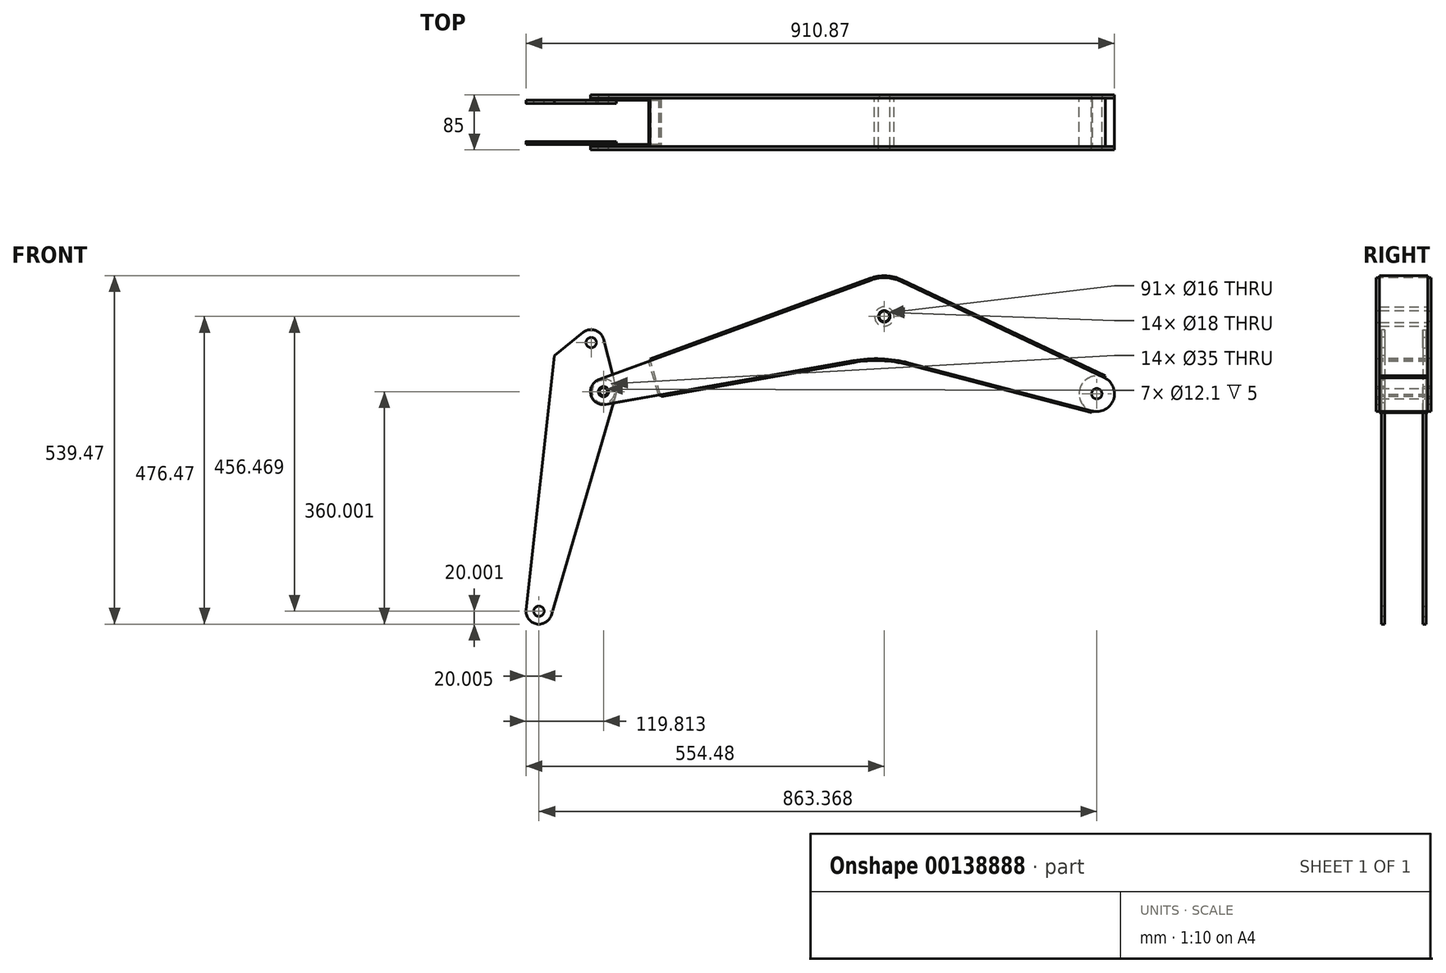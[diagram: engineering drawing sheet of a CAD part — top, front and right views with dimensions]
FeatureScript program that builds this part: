
annotation { "Feature Type Name" : "Feature", "Feature Type Description" : "" }
export const myFeature = defineFeature(function(context is Context, id is Id, definition is map)
    precondition{}
    {
        {
            var Q0;
            Q0=qCreatedBy(makeId("Front.planeOp"),FACE);
            var sketch = newSketch(context, id + "F0", { "sketchPlane" : qUnion([Q0])});
            skCircle(sketch, "E0", {"center": v(0, 0) * mm, "radius": 60 * mm});
            skLineSegment(sketch, "E1", {"start": v(0, 0) * mm, "end": v(-434.67, -116.47) * mm, "construction": true});
            skCircle(sketch, "E2", {"center": v(-434.67, -116.47) * mm, "radius": 20 * mm});
            skLineSegment(sketch, "E3", {"start": v(0, 0) * mm, "end": v(328.9, -119.7) * mm, "construction": true});
            skCircle(sketch, "E4", {"center": v(328.9, -119.7) * mm, "radius": 27.5 * mm});
            skLineSegment(sketch, "E5", {"start": v(-20.62, 56.35) * mm, "end": v(-441.54, -97.69) * mm});
            skLineSegment(sketch, "E6", {"start": v(-47.69, -68.42) * mm, "end": v(-431.19, -136.16) * mm});
            skLineSegment(sketch, "E7", {"start": v(37.7, -71.9) * mm, "end": v(321.93, -146.31) * mm});
            skLineSegment(sketch, "E8", {"start": v(25.67, 54.23) * mm, "end": v(340.66, -94.85) * mm});
            skPoint(sketch, "E9", {"position": v(-4.61, -60.81) * mm});
            skPoint(sketch, "E10.orphan", {"position": v(0, -60) * mm});
            skArc(sketch, "E11.filletArc", {"start": v(37.7, -71.9) * mm, "mid": v(-4.8, -65.54) * mm, "end": v(-47.69, -68.42) * mm});
            skCircle(sketch, "E12", {"center": v(0, 0) * mm, "radius": 8 * mm});
            skCircle(sketch, "E13", {"center": v(328.9, -119.7) * mm, "radius": 8 * mm});
            skCircle(sketch, "E14", {"center": v(-434.67, -116.47) * mm, "radius": 8 * mm});
            skCircle(sketch, "E15", {"center": v(328.9, -119.7) * mm, "radius": 6.05 * mm});
            skCircle(sketch, "E16", {"center": v(328.9, -119.7) * mm, "radius": 22.5 * mm});
            skCircle(sketch, "E17", {"center": v(-434.67, -116.47) * mm, "radius": 6.05 * mm});
            skCircle(sketch, "E18", {"center": v(-434.67, -116.47) * mm, "radius": 17.5 * mm});
            skCircle(sketch, "E19", {"center": v(0, 0) * mm, "radius": 6.05 * mm});
            skCircle(sketch, "E20", {"center": v(0, 0) * mm, "radius": 9 * mm});
            skCircle(sketch, "E21", {"center": v(0, 0) * mm, "radius": 15 * mm});
            skSolve(sketch);
        }
        {
            var Q0;
            Q0 = qSketchRegion(id + "FwEDvxsUyDdSrLS_0", true);
            var Q1;
            Q1=makeQuery(id+"F0.imprint","IMPRINT",FACE,{"disambiguationData":[TD([[makeQuery(id+"F0.imprint","IMPRINT",EDGE,{"derivedFrom":sQuery(id+"F0.wireOp",EDGE,"E14")}),-1.0]])]});
            extrude(context, id + "F1", {"entities" : qUnion([Q0, Q1]), "depth" : 5 * mm});
        }
        {
            var Q0;
            Q0 = qSketchRegion(id + "F0", true);
            var Q1;
            Q1=makeQuery(id+"F0.imprint","IMPRINT",FACE,{"disambiguationData":[TD([[makeQuery(id+"F0.imprint","IMPRINT",EDGE,{"derivedFrom":sQuery(id+"F0.wireOp",EDGE,"E13")}),-1.0]])]});
            var Q2;
            Q2=makeQuery(id+"F0.imprint","IMPRINT",FACE,{"disambiguationData":[TD([[makeQuery(id+"F0.imprint","IMPRINT",EDGE,{"derivedFrom":sQuery(id+"F0.wireOp",EDGE,"E12")}),-1.0]])]});
            var Q3;
            Q3=makeQuery(id+"F0.imprint","IMPRINT",FACE,{"disambiguationData":[TD([[makeQuery(id+"F0.imprint","IMPRINT",EDGE,{"derivedFrom":sQuery(id+"F0.wireOp",EDGE,"E14")}),-1.0]])]});
            var Q4;
            Q4=makeQuery(id+"F0.imprint","IMPRINT",FACE,{"disambiguationData":[TD([[makeQuery(id+"F0.imprint","IMPRINT",EDGE,{"derivedFrom":sQuery(id+"F0.wireOp",EDGE,"E20")}),-1.0]])]});
            extrude(context, id + "F2", {"entities" : qUnion([Q0, Q1, Q2, Q3, Q4]), "oppositeDirection" : true, "depth" : 5 * mm});
        }
        {
            var Q0;
            Q0=makeQuery(id+"F2.opExtrude","CAP_FACE",FACE,{"disambiguationData":[OSD([sQuery(id+"F0.wireOp",EDGE,"E0"),sQuery(id+"F0.wireOp",EDGE,"E2"),sQuery(id+"F0.wireOp",EDGE,"E4"),sQuery(id+"F0.wireOp",EDGE,"E5"),sQuery(id+"F0.wireOp",EDGE,"E6"),sQuery(id+"F0.wireOp",EDGE,"E7"),sQuery(id+"F0.wireOp",EDGE,"E8"),sQuery(id+"F0.wireOp",EDGE,"E11.filletArc"),sQuery(id+"F0.wireOp",EDGE,"E12"),sQuery(id+"F0.wireOp",EDGE,"E13"),sQuery(id+"F0.wireOp",EDGE,"E14")])],"isStart":true});
            cPlane(context, id + "F3", {"entities" : qUnion([Q0]), "cplaneType" : CPlaneType.OFFSET, "offset" : 75 * mm, "width" : 150 * mm, "height" : 150 * mm});
        }
        {
            var Q0;
            Q0=qCreatedBy(id+"F3.planeOp",FACE);
            var sketch = newSketch(context, id + "F4", { "sketchPlane" : qUnion([Q0])});
            skArc(sketch, "E22.0.0", {"start": v(25.67, 54.23) * mm, "mid": v(2.74, 59.94) * mm, "end": v(-20.62, 56.35) * mm});
            skLineSegment(sketch, "E22.0.1", {"start": v(-20.62, 56.35) * mm, "end": v(-441.54, -97.69) * mm});
            skArc(sketch, "E22.0.2", {"start": v(-441.54, -97.69) * mm, "mid": v(-453.98, -121.66) * mm, "end": v(-431.19, -136.16) * mm});
            skLineSegment(sketch, "E22.0.3", {"start": v(-431.19, -136.16) * mm, "end": v(-47.69, -68.42) * mm});
            skArc(sketch, "E22.0.4", {"start": v(-47.69, -68.42) * mm, "mid": v(-4.8, -65.54) * mm, "end": v(37.7, -71.9) * mm});
            skLineSegment(sketch, "E22.0.5", {"start": v(37.7, -71.9) * mm, "end": v(321.93, -146.31) * mm});
            skArc(sketch, "E22.0.6", {"start": v(321.93, -146.31) * mm, "mid": v(354.73, -129.11) * mm, "end": v(340.66, -94.85) * mm});
            skLineSegment(sketch, "E22.0.7", {"start": v(340.66, -94.85) * mm, "end": v(25.67, 54.23) * mm});
            skCircle(sketch, "E23.0", {"center": v(-434.67, -116.47) * mm, "radius": 8 * mm});
            skCircle(sketch, "E24.0", {"center": v(0, 0) * mm, "radius": 8 * mm});
            skCircle(sketch, "E24.1", {"center": v(328.9, -119.7) * mm, "radius": 8 * mm});
            skCircle(sketch, "E25.0", {"center": v(0, 0) * mm, "radius": 6.05 * mm});
            skCircle(sketch, "E25.1", {"center": v(0, 0) * mm, "radius": 9 * mm});
            skCircle(sketch, "E26.0", {"center": v(328.9, -119.7) * mm, "radius": 6.05 * mm});
            skCircle(sketch, "E26.1", {"center": v(328.9, -119.7) * mm, "radius": 22.5 * mm});
            skCircle(sketch, "E27.0", {"center": v(-434.67, -116.47) * mm, "radius": 6.05 * mm});
            skCircle(sketch, "E27.1", {"center": v(-434.67, -116.47) * mm, "radius": 17.5 * mm});
            skSolve(sketch);
        }
        {
            var Q0;
            Q0 = qSketchRegion(id + "F4", true);
            var Q1;
            Q1=makeQuery(id+"F4.imprint","IMPRINT",FACE,{"disambiguationData":[TD([[makeQuery(id+"F4.imprint","IMPRINT",EDGE,{"derivedFrom":sQuery(id+"F4.wireOp",EDGE,"E24.1")}),-1.0]])]});
            var Q2;
            Q2=makeQuery(id+"F4.imprint","IMPRINT",FACE,{"disambiguationData":[TD([[makeQuery(id+"F4.imprint","IMPRINT",EDGE,{"derivedFrom":sQuery(id+"F4.wireOp",EDGE,"E23.0")}),-1.0]])]});
            extrude(context, id + "F5", {"entities" : qUnion([Q0, Q1, Q2]), "depth" : 5 * mm});
        }
        {
            var Q0;
            Q0=makeQuery(id+"F0.imprint","IMPRINT",FACE,{"disambiguationData":[TD([[makeQuery(id+"F0.imprint","IMPRINT",EDGE,{"derivedFrom":sQuery(id+"F0.wireOp",EDGE,"E13")}),-1.0]])]});
            var Q1;
            Q1=makeQuery(id+"F0.imprint","IMPRINT",FACE,{"disambiguationData":[TD([[makeQuery(id+"F0.imprint","IMPRINT",EDGE,{"derivedFrom":sQuery(id+"F0.wireOp",EDGE,"E16")}),-1.0]])]});
            var Q2;
            Q2=makeQuery(id+"F5.opExtrude","CAP_FACE",FACE,{"disambiguationData":[OSD([sQuery(id+"F4.wireOp",EDGE,"E22.0.0"),sQuery(id+"F4.wireOp",EDGE,"E22.0.1"),sQuery(id+"F4.wireOp",EDGE,"E22.0.2"),sQuery(id+"F4.wireOp",EDGE,"E22.0.3"),sQuery(id+"F4.wireOp",EDGE,"E22.0.4"),sQuery(id+"F4.wireOp",EDGE,"E22.0.5"),sQuery(id+"F4.wireOp",EDGE,"E22.0.6"),sQuery(id+"F4.wireOp",EDGE,"E22.0.7"),sQuery(id+"F4.wireOp",EDGE,"E23.0"),sQuery(id+"F4.wireOp",EDGE,"E24.1"),sQuery(id+"F4.wireOp",EDGE,"E25.1")])],"isStart":true});
            extrude(context, id + "F6", {"entities" : qUnion([Q0, Q1]), "endBound" : BoundingType.UP_TO_SURFACE, "endBoundEntityFace" : qUnion([Q2]), "depth" : 25 * mm});
        }
        {
            var Q0;
            Q0=makeQuery(id+"F0.imprint","IMPRINT",FACE,{"disambiguationData":[TD([[makeQuery(id+"F0.imprint","IMPRINT",EDGE,{"derivedFrom":sQuery(id+"F0.wireOp",EDGE,"E20")}),-1.0]])]});
            var Q1;
            Q1=makeQuery(id+"F5.opExtrude","CAP_FACE",FACE,{"disambiguationData":[OSD([sQuery(id+"F4.wireOp",EDGE,"E22.0.0"),sQuery(id+"F4.wireOp",EDGE,"E22.0.1"),sQuery(id+"F4.wireOp",EDGE,"E22.0.2"),sQuery(id+"F4.wireOp",EDGE,"E22.0.3"),sQuery(id+"F4.wireOp",EDGE,"E22.0.4"),sQuery(id+"F4.wireOp",EDGE,"E22.0.5"),sQuery(id+"F4.wireOp",EDGE,"E22.0.6"),sQuery(id+"F4.wireOp",EDGE,"E22.0.7"),sQuery(id+"F4.wireOp",EDGE,"E23.0"),sQuery(id+"F4.wireOp",EDGE,"E24.1"),sQuery(id+"F4.wireOp",EDGE,"E25.1")])],"isStart":true});
            extrude(context, id + "F7", {"entities" : qUnion([Q0]), "endBound" : BoundingType.UP_TO_SURFACE, "endBoundEntityFace" : qUnion([Q1]), "depth" : 25 * mm});
        }
        {
            var Q0;
            Q0=makeQuery(id+"F4.imprint","IMPRINT",FACE,{"disambiguationData":[TD([[makeQuery(id+"F4.imprint","IMPRINT",EDGE,{"derivedFrom":sQuery(id+"F4.wireOp",EDGE,"E22.0.0")}),1.0]])]});
            var sketch = newSketch(context, id + "F8", { "sketchPlane" : qUnion([Q0])});
            skLineSegment(sketch, "E28.0", {"start": v(-20.62, 56.35) * mm, "end": v(-441.54, -97.69) * mm});
            skArc(sketch, "E28.1", {"start": v(25.67, 54.23) * mm, "mid": v(2.74, 59.94) * mm, "end": v(-20.62, 56.35) * mm});
            skLineSegment(sketch, "E28.2", {"start": v(340.66, -94.85) * mm, "end": v(25.67, 54.23) * mm});
            skLineSegment(sketch, "E28.3", {"start": v(37.7, -71.9) * mm, "end": v(321.93, -146.31) * mm});
            skArc(sketch, "E28.4", {"start": v(-47.69, -68.42) * mm, "mid": v(-4.8, -65.54) * mm, "end": v(37.7, -71.9) * mm});
            skLineSegment(sketch, "E28.5", {"start": v(-431.19, -136.16) * mm, "end": v(-47.69, -68.42) * mm});
            skLineSegment(sketch, "E29.0", {"start": v(-21.65, 59.16) * mm, "end": v(-362.75, -65.66) * mm});
            skArc(sketch, "E29.1", {"start": v(26.95, 56.94) * mm, "mid": v(2.87, 62.93) * mm, "end": v(-21.65, 59.16) * mm});
            skLineSegment(sketch, "E29.2", {"start": v(341.94, -92.14) * mm, "end": v(26.95, 56.94) * mm});
            skLineSegment(sketch, "E30.0", {"start": v(36.94, -74.8) * mm, "end": v(321.17, -149.21) * mm});
            skArc(sketch, "E30.1", {"start": v(-47.16, -71.38) * mm, "mid": v(-4.93, -68.54) * mm, "end": v(36.94, -74.8) * mm});
            skLineSegment(sketch, "E30.2", {"start": v(-345.67, -124.1) * mm, "end": v(-47.16, -71.38) * mm});
            skLineSegment(sketch, "E31", {"start": v(341.94, -92.14) * mm, "end": v(340.66, -94.85) * mm});
            skLineSegment(sketch, "E32", {"start": v(321.93, -146.31) * mm, "end": v(321.17, -149.21) * mm});
            skLineSegment(sketch, "E33", {"start": v(-362.75, -65.66) * mm, "end": v(-361.72, -68.48) * mm});
            skLineSegment(sketch, "E34", {"start": v(-346.19, -121.15) * mm, "end": v(-345.67, -124.1) * mm});
            skLineSegment(sketch, "E35", {"start": v(-362.75, -65.66) * mm, "end": v(-345.67, -124.1) * mm});
            skLineSegment(sketch, "E36", {"start": v(-362.75, -65.66) * mm, "end": v(-365.56, -66.69) * mm});
            skLineSegment(sketch, "E37", {"start": v(-345.67, -124.1) * mm, "end": v(-348.62, -124.63) * mm});
            skLineSegment(sketch, "E38", {"start": v(-348.62, -124.63) * mm, "end": v(-365.56, -66.69) * mm});
            skSolve(sketch);
        }
        {
            var Q0;
            {var subQ0=sQuery(id+"F8.wireOp",EDGE,"E28.1");Q0=makeQuery(id+"F8.imprint","IMPRINT",FACE,{"disambiguationData":[TD([[makeQuery(id+"F8.imprint","IMPRINT",EDGE,{"derivedFrom":subQ0}),-1.0]])]});}
            var Q1;
            Q1=makeQuery(id+"F2.opExtrude","CAP_FACE",FACE,{"disambiguationData":[OSD([sQuery(id+"F0.wireOp",EDGE,"E0"),sQuery(id+"F0.wireOp",EDGE,"E2"),sQuery(id+"F0.wireOp",EDGE,"E4"),sQuery(id+"F0.wireOp",EDGE,"E5"),sQuery(id+"F0.wireOp",EDGE,"E6"),sQuery(id+"F0.wireOp",EDGE,"E7"),sQuery(id+"F0.wireOp",EDGE,"E8"),sQuery(id+"F0.wireOp",EDGE,"E11.filletArc"),sQuery(id+"F0.wireOp",EDGE,"E12"),sQuery(id+"F0.wireOp",EDGE,"E13"),sQuery(id+"F0.wireOp",EDGE,"E14")])],"isStart":true});
            extrude(context, id + "F9", {"entities" : qUnion([Q0]), "endBound" : BoundingType.UP_TO_SURFACE, "oppositeDirection" : true, "endBoundEntityFace" : qUnion([Q1]), "depth" : 25 * mm});
        }
        {
            var Q0;
            Q0=makeQuery(id+"F8.imprint","IMPRINT",FACE,{"disambiguationData":[TD([[makeQuery(id+"F8.imprint","IMPRINT",EDGE,{"derivedFrom":sQuery(id+"F8.wireOp",EDGE,"E28.3")}),-1.0]])]});
            var Q1;
            Q1=makeQuery(id+"F2.opExtrude","CAP_FACE",FACE,{"disambiguationData":[OSD([sQuery(id+"F0.wireOp",EDGE,"E0"),sQuery(id+"F0.wireOp",EDGE,"E2"),sQuery(id+"F0.wireOp",EDGE,"E4"),sQuery(id+"F0.wireOp",EDGE,"E5"),sQuery(id+"F0.wireOp",EDGE,"E6"),sQuery(id+"F0.wireOp",EDGE,"E7"),sQuery(id+"F0.wireOp",EDGE,"E8"),sQuery(id+"F0.wireOp",EDGE,"E11.filletArc"),sQuery(id+"F0.wireOp",EDGE,"E12"),sQuery(id+"F0.wireOp",EDGE,"E13"),sQuery(id+"F0.wireOp",EDGE,"E14")])],"isStart":true});
            extrude(context, id + "F10", {"entities" : qUnion([Q0]), "endBound" : BoundingType.UP_TO_SURFACE, "oppositeDirection" : true, "endBoundEntityFace" : qUnion([Q1]), "depth" : 25 * mm});
        }
        {
            var Q0;
            {var subQ0=sQuery(id+"F8.wireOp",EDGE,"E38");var subQ1=sQuery(id+"F8.wireOp",EDGE,"E28.0");var subQ2=makeQuery(id+"F8.imprint","INTERSECT",VERTEX,{"derivedFrom":[subQ1,subQ0]});Q0=makeQuery(id+"F8.imprint","IMPRINT",FACE,{"disambiguationData":[TD([[makeQuery(id+"F8.imprint","IMPRINT",EDGE,{"disambiguationData":[TD([[subQ2,1.0]])],"derivedFrom":subQ1}),1.0]])]});}
            var Q1;
            Q1=makeQuery(id+"F2.opExtrude","CAP_FACE",FACE,{"disambiguationData":[OSD([sQuery(id+"F0.wireOp",EDGE,"E0"),sQuery(id+"F0.wireOp",EDGE,"E2"),sQuery(id+"F0.wireOp",EDGE,"E4"),sQuery(id+"F0.wireOp",EDGE,"E5"),sQuery(id+"F0.wireOp",EDGE,"E6"),sQuery(id+"F0.wireOp",EDGE,"E7"),sQuery(id+"F0.wireOp",EDGE,"E8"),sQuery(id+"F0.wireOp",EDGE,"E11.filletArc"),sQuery(id+"F0.wireOp",EDGE,"E12"),sQuery(id+"F0.wireOp",EDGE,"E13"),sQuery(id+"F0.wireOp",EDGE,"E14")])],"isStart":true});
            extrude(context, id + "F11", {"entities" : qUnion([Q0]), "endBound" : BoundingType.UP_TO_SURFACE, "oppositeDirection" : true, "endBoundEntityFace" : qUnion([Q1]), "depth" : 25 * mm});
        }
        {
            var Q0;
            {var subQ0=makeQuery(id+"F4.imprint","IMPRINT",EDGE,{"derivedFrom":sQuery(id+"F4.wireOp",EDGE,"E22.0.2")});Q0=makeQuery(id+"F8.imprint","IMPRINT",FACE,{"disambiguationData":[TD([[makeQuery(id+"F8.imprint","IMPRINT",EDGE,{"derivedFrom":subQ0}),1.0]])]});}
            var Q1;
            Q1=makeQuery(id+"F4.imprint","IMPRINT",FACE,{"disambiguationData":[TD([[makeQuery(id+"F4.imprint","IMPRINT",EDGE,{"derivedFrom":sQuery(id+"F4.wireOp",EDGE,"E23.0")}),-1.0]])]});
            extrude(context, id + "F12", {"entities" : qUnion([Q0, Q1]), "oppositeDirection" : true, "depth" : 3 * mm});
        }
        {
            var Q0;
            {var subQ0=sQuery(id+"F0.wireOp",EDGE,"E5");Q0=makeQuery(id+"F0.imprint","IMPRINT",FACE,{"disambiguationData":[TD([[makeQuery(id+"F0.imprint","IMPRINT",EDGE,{"derivedFrom":subQ0}),1.0]])]});}
            var sketch = newSketch(context, id + "F13", { "sketchPlane" : qUnion([Q0])});
            skLineSegment(sketch, "E39.0", {"start": v(-364.72, -69.58) * mm, "end": v(-349.47, -121.73) * mm});
            skLineSegment(sketch, "E39.1", {"start": v(-20.62, 56.35) * mm, "end": v(-441.54, -97.69) * mm});
            skLineSegment(sketch, "E39.2", {"start": v(-47.69, -68.42) * mm, "end": v(-431.19, -136.16) * mm});
            skCircle(sketch, "E39.3", {"center": v(-434.67, -116.47) * mm, "radius": 20 * mm});
            skSolve(sketch);
        }
        {
            var Q0;
            {var subQ0=sQuery(id+"F13.wireOp",EDGE,"E39.0");Q0=makeQuery(id+"F13.imprint","IMPRINT",FACE,{"disambiguationData":[TD([[makeQuery(id+"F13.imprint","IMPRINT",EDGE,{"derivedFrom":subQ0}),-1.0]])]});}
            var Q1;
            Q1=makeQuery(id+"F0.imprint","IMPRINT",FACE,{"disambiguationData":[TD([[makeQuery(id+"F0.imprint","IMPRINT",EDGE,{"derivedFrom":sQuery(id+"F0.wireOp",EDGE,"E14")}),-1.0]])]});
            var Q2;
            Q2=makeQuery(id+"F0.imprint","IMPRINT",FACE,{"disambiguationData":[TD([[makeQuery(id+"F0.imprint","IMPRINT",EDGE,{"derivedFrom":sQuery(id+"F0.wireOp",EDGE,"E18")}),-1.0]])]});
            extrude(context, id + "F14", {"entities" : qUnion([Q0, Q1, Q2]), "depth" : 3 * mm});
        }
        {
            var Q0;
            Q0=makeQuery(id+"F12.opExtrude","CAP_FACE",FACE,{"disambiguationData":[OSD([sQuery(id+"F4.wireOp",EDGE,"E22.0.2"),sQuery(id+"F4.wireOp",EDGE,"E27.1"),sQuery(id+"F8.wireOp",EDGE,"E28.0"),sQuery(id+"F8.wireOp",EDGE,"E28.5"),sQuery(id+"F8.wireOp",EDGE,"E38")])],"isStart":false});
            cPlane(context, id + "F15", {"entities" : qUnion([Q0]), "cplaneType" : CPlaneType.OFFSET, "offset" : 0 * mm, "width" : 150 * mm, "height" : 150 * mm});
        }
        {
            var Q0;
            Q0=qCreatedBy(id+"F15.planeOp",FACE);
            var sketch = newSketch(context, id + "F16", { "sketchPlane" : qUnion([Q0])});
            skCircle(sketch, "E40.0", {"center": v(434.67, -116.47) * mm, "radius": 6.05 * mm});
            skCircle(sketch, "E40.1", {"center": v(434.67, -116.47) * mm, "radius": 8 * mm});
            skCircle(sketch, "E40.2", {"center": v(434.67, -116.47) * mm, "radius": 17.5 * mm});
            skCircle(sketch, "E40.3", {"center": v(434.67, -116.47) * mm, "radius": 20 * mm});
            skCircle(sketch, "E40.4", {"center": v(453.67, -40.47) * mm, "radius": 20 * mm});
            skLineSegment(sketch, "E40.5", {"start": v(434.26, -35.62) * mm, "end": v(415.26, -111.62) * mm});
            skCircle(sketch, "E40.6", {"center": v(534.48, -456.47) * mm, "radius": 20 * mm});
            skLineSegment(sketch, "E40.7", {"start": v(466.16, -24.85) * mm, "end": v(510.67, -60.47) * mm});
            skLineSegment(sketch, "E40.8", {"start": v(510.67, -60.47) * mm, "end": v(554.35, -454.26) * mm});
            skLineSegment(sketch, "E40.9", {"start": v(515.29, -462.1) * mm, "end": v(415.48, -122.1) * mm});
            skCircle(sketch, "E40.10", {"center": v(453.67, -40.47) * mm, "radius": 8 * mm});
            skCircle(sketch, "E40.11", {"center": v(534.48, -456.47) * mm, "radius": 8 * mm});
            skSolve(sketch);
        }
        {
            var Q0;
            Q0 = qSketchRegion(id + "F16", true);
            var Q1;
            Q1=makeQuery(id+"F16.imprint","IMPRINT",FACE,{"disambiguationData":[TD([[makeQuery(id+"F16.imprint","IMPRINT",EDGE,{"derivedFrom":sQuery(id+"F16.wireOp",EDGE,"E40.1")}),1.0]])]});
            extrude(context, id + "F17", {"entities" : qUnion([Q0, Q1]), "depth" : 5 * mm});
        }
        {
            var Q0;
            Q0=makeQuery(id+"F1.opExtrude","SWEPT_BODY",BODY,{"disambiguationData":[OSD([sQuery(id+"F0.wireOp",EDGE,"E14"),sQuery(id+"F0.wireOp",EDGE,"E18")])]});
            deleteBodies(context, id + "F18", {"entities" : qUnion([Q0])});
        }
        {
            var Q0;
            Q0=makeQuery(id+"F14.opExtrude","CAP_FACE",FACE,{"disambiguationData":[OSD([sQuery(id+"F0.wireOp",EDGE,"E2"),sQuery(id+"F0.wireOp",EDGE,"E14")])],"isStart":false});
            var sketch = newSketch(context, id + "F19", { "sketchPlane" : qUnion([Q0])});
            skCircle(sketch, "E41.0", {"center": v(-434.67, -116.47) * mm, "radius": 6.05 * mm});
            skCircle(sketch, "E41.1", {"center": v(-434.67, -116.47) * mm, "radius": 8 * mm});
            skCircle(sketch, "E41.2", {"center": v(-434.67, -116.47) * mm, "radius": 17.5 * mm});
            skCircle(sketch, "E41.3", {"center": v(-434.67, -116.47) * mm, "radius": 20 * mm});
            skCircle(sketch, "E41.4", {"center": v(-453.67, -40.47) * mm, "radius": 20 * mm});
            skLineSegment(sketch, "E41.5", {"start": v(-434.26, -35.62) * mm, "end": v(-415.26, -111.62) * mm});
            skCircle(sketch, "E41.6", {"center": v(-534.48, -456.47) * mm, "radius": 20 * mm});
            skLineSegment(sketch, "E41.7", {"start": v(-466.16, -24.85) * mm, "end": v(-510.67, -60.47) * mm});
            skLineSegment(sketch, "E41.8", {"start": v(-510.67, -60.47) * mm, "end": v(-554.35, -454.26) * mm});
            skLineSegment(sketch, "E41.9", {"start": v(-515.29, -462.1) * mm, "end": v(-415.48, -122.1) * mm});
            skCircle(sketch, "E41.10", {"center": v(-453.67, -40.47) * mm, "radius": 8 * mm});
            skCircle(sketch, "E41.11", {"center": v(-534.48, -456.47) * mm, "radius": 8 * mm});
            skSolve(sketch);
        }
        {
            var Q0;
            Q0 = qSketchRegion(id + "F19", true);
            var Q1;
            Q1=makeQuery(id+"F19.imprint","IMPRINT",FACE,{"disambiguationData":[TD([[makeQuery(id+"F19.imprint","IMPRINT",EDGE,{"derivedFrom":sQuery(id+"F19.wireOp",EDGE,"E41.1")}),-1.0]])]});
            extrude(context, id + "F20", {"entities" : qUnion([Q0, Q1]), "depth" : 5 * mm});
        }
    });
